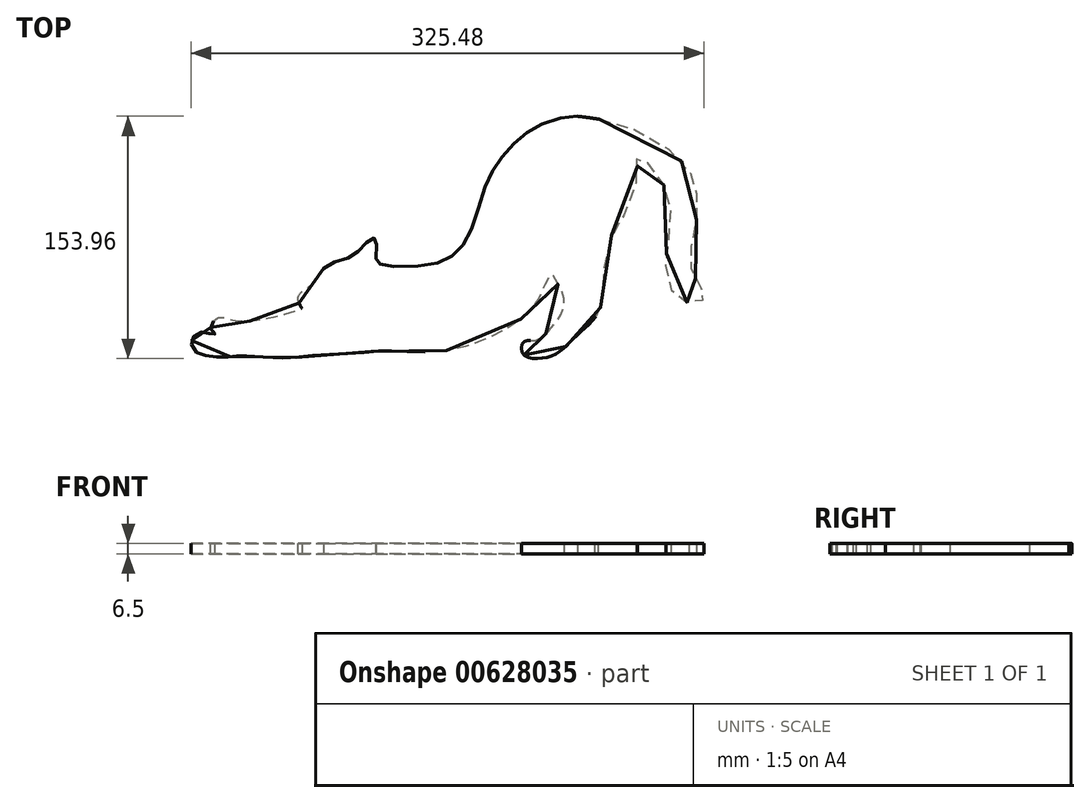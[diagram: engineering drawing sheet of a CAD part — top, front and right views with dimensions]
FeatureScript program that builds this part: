
annotation { "Feature Type Name" : "Feature", "Feature Type Description" : "" }
export const myFeature = defineFeature(function(context is Context, id is Id, definition is map)
    precondition{}
    {
        {
            var Q0;
            Q0=qCreatedBy(makeId("Top.planeOp"),FACE);
            var sketch = newSketch(context, id + "F0", { "sketchPlane" : qUnion([Q0])});
            skFitSpline(sketch, "E0", {"points": [v(71.65, 98.65) * mm, v(91.63, 95.05) * mm, v(114.98, 83.6) * mm, v(127.03, 70.5) * mm, v(129.57, 63.62) * mm, v(130.17, 53.22) * mm, v(128.45, 39.9) * mm, v(126.5, 30.54) * mm, v(127.85, 22.54) * mm, v(131.97, 15.13) * mm, v(133.24, 11.53) * mm, v(133.24, 9.21) * mm, v(130.62, 7.87) * mm, v(125.6, 7.57) * mm, v(120.67, 9.89) * mm, v(117, 15.5) * mm, v(114.98, 28.22) * mm, v(116.48, 38.85) * mm, v(117.37, 54.2) * mm, v(113.26, 66.24) * mm, v(106.6, 75.3) * mm, v(102.93, 77.4) * mm, v(100.61, 77.92) * mm, v(100.84, 76.72) * mm, v(99.71, 63.02) * mm, v(92.23, 46.7) * mm, v(87.36, 37.65) * mm, v(84.37, 20.22) * mm, v(83.4, 6.52) * mm, v(81.53, 1.73) * mm, v(76.96, -3.5) * mm, v(71.27, -8.6) * mm, v(64.24, -15.4) * mm, v(59.6, -18.33) * mm, v(53.61, -19.67) * mm, v(48.08, -19.22) * mm, v(44.7, -16.83) * mm, v(44.88, -12.4) * mm, v(47.01, -10.98) * mm, v(49.27, -11.07) * mm, v(52.64, -10.32) * mm, v(60.12, -3.43) * mm, v(64.91, 4.43) * mm, v(64.84, 11.31) * mm, v(61.17, 18.42) * mm, v(58.97, 21.39) * mm, v(52.16, 8.59) * mm, v(40.52, -2.98) * mm, v(24.13, -11.37) * mm, v(6.02, -16) * mm, v(-13.97, -16.16) * mm, v(-25.2, -16.08) * mm, v(-38.81, -17.28) * mm, v(-57, -18.25) * mm, v(-69.12, -19.37) * mm, v(-89.03, -18.55) * mm, v(-94.8, -18.4) * mm, v(-99.8, -18.92) * mm, v(-107.81, -18.63) * mm, v(-113.35, -17.28) * mm, v(-116.72, -13.54) * mm, v(-115.9, -9.12) * mm, v(-112.15, -6.88) * mm, v(-108.71, -7.32) * mm, v(-105.27, -8) * mm, v(-106.76, -6.58) * mm, v(-107.44, -3.73) * mm, v(-104.3, 0) * mm, v(-99.65, -0.07) * mm, v(-95.46, -1.11) * mm, v(-85.8, -1.04) * mm, v(-68.52, 2.7) * mm, v(-62.68, 4.8) * mm, v(-63.06, 5.17) * mm, v(-64.7, 9.06) * mm, v(-64.33, 11.24) * mm, v(-62.83, 12.96) * mm, v(-57.6, 17) * mm, v(-52.2, 24.26) * mm], "startDerivative": vector(939.84, -111.17) * mm, "endDerivative": vector(455.8, 390.68) * mm});
            skFitSpline(sketch, "E1", {"points": [v(-52.2, 24.26) * mm, v(-48.39, 26.88) * mm, v(-42.25, 28.9) * mm, v(-37.61, 30.77) * mm, v(-34.25, 33.7) * mm, v(-30.88, 37.43) * mm, v(-28.56, 39.15) * mm, v(-27.14, 38.7) * mm, v(-26.54, 37.5) * mm, v(-26.39, 35.49) * mm, v(-26.69, 28.75) * mm, v(-25.94, 27.33) * mm, v(-24.74, 26.43) * mm, v(-20.92, 25.38) * mm, v(-3.94, 25.68) * mm, v(6.24, 27.93) * mm, v(12.9, 32.27) * mm, v(17.7, 38.7) * mm, v(22.63, 51.2) * mm, v(27.12, 65.87) * mm, v(31.39, 73.95) * mm, v(37.15, 81.66) * mm, v(44.63, 88.85) * mm, v(51.44, 93.41) * mm, v(62.74, 97.68) * mm, v(71.65, 98.65) * mm, v(80.3, 97.52) * mm, v(82.1, 97.22) * mm, v(82.19, 97.2) * mm], "startDerivative": vector(108.34, 89.27) * mm, "endDerivative": vector(14.58, -2.32) * mm});
            skSolve(sketch);
        }
        {
            var Q0;
            {var subQ0=sQuery(id+"F0.wireOp",EDGE,"E1");var subQ1=sQuery(id+"F0.wireOp",EDGE,"E0");var subQ2=makeQuery(id+"F0.imprint","INTERSECT",VERTEX,{"disambiguationData":[OD(0.0)],"derivedFrom":[subQ1,subQ0]});Q0=makeQuery(id+"F0.imprint","IMPRINT",FACE,{"disambiguationData":[TD([[makeQuery(id+"F0.imprint","IMPRINT",EDGE,{"disambiguationData":[TD([[subQ2,-1.0]])],"derivedFrom":subQ1}),-1.0]])]});}
            extrude(context, id + "F1", {"entities" : qUnion([Q0]), "depth" : 5 * mm, "offsetDistance" : 25 * mm});
        }
        {
            var Q0;
            Q0=makeQuery(id+"F1.opExtrude","CAP_FACE",FACE,{"disambiguationData":[OSD([sQuery(id+"F0.wireOp",EDGE,"E0"),sQuery(id+"F0.wireOp",EDGE,"E1")])],"isStart":false});
            var sketch = newSketch(context, id + "F2", { "sketchPlane" : qUnion([Q0])});
            skLineSegment(sketch, "E2", {"start": v(-70.8, 17.52) * mm, "end": v(-33.19, 42.23) * mm});
            skSolve(sketch);
        }
        {
            var Q0;
            Q0=makeQuery(id+"F1.opExtrude","SWEPT_BODY",BODY,{"disambiguationData":[OSD([sQuery(id+"F0.wireOp",EDGE,"E0"),sQuery(id+"F0.wireOp",EDGE,"E1")])]});
            var Q1;
            Q1=sQuery(id+"F2.wireOp",VERTEX,"E2.start");
            transform(context, id + "F3", {"entities" : qUnion([Q0]), "transformType" : TransformType.SCALE_UNIFORMLY, "scale" : 1.3, "scalePoint" : qUnion([Q1]), "makeCopy" : false});
        }
    });
